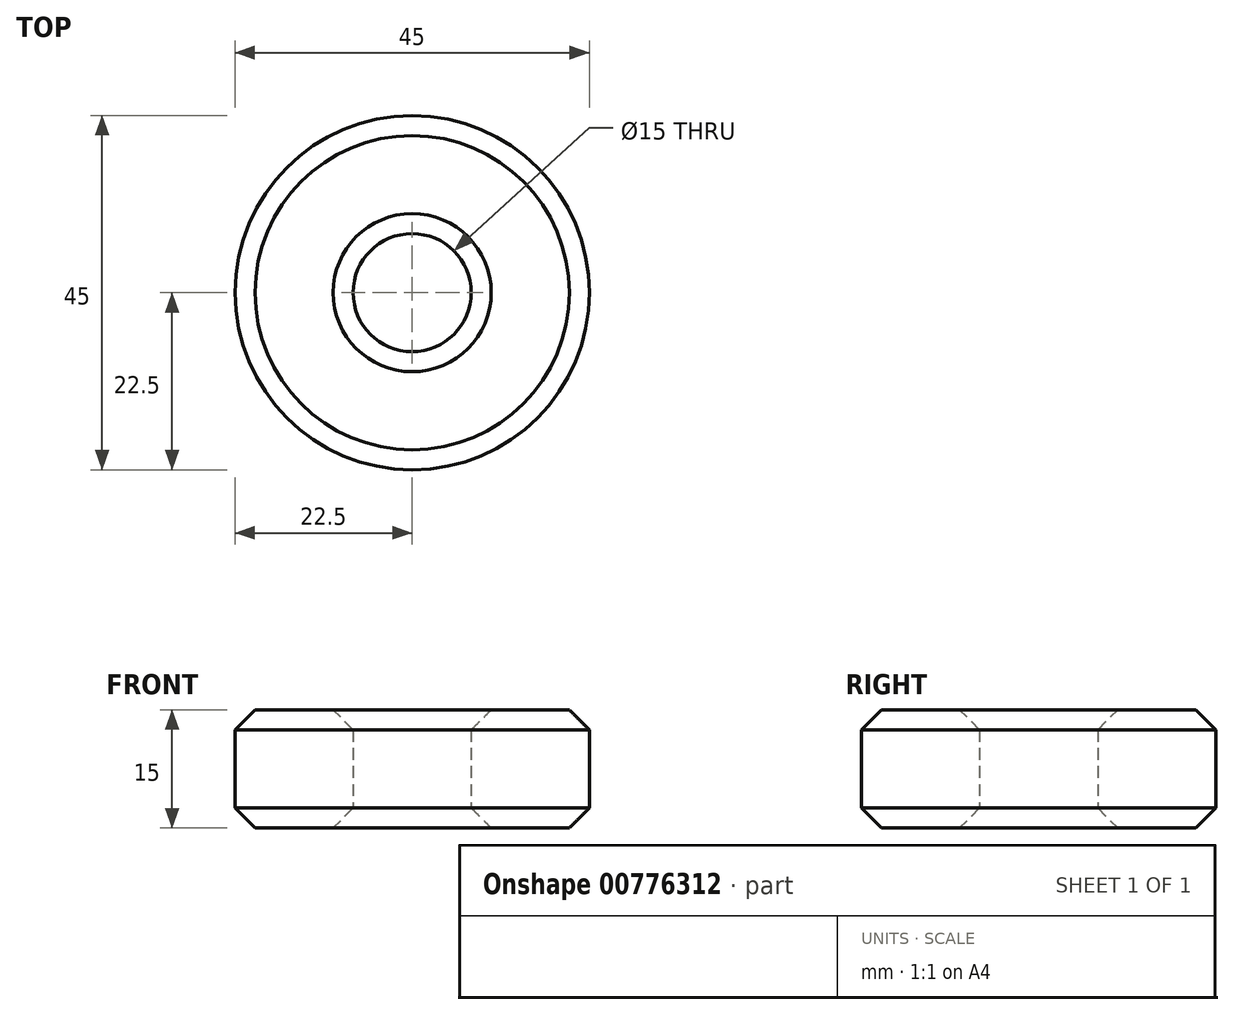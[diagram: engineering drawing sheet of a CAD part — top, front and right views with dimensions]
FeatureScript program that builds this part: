
annotation { "Feature Type Name" : "Feature", "Feature Type Description" : "" }
export const myFeature = defineFeature(function(context is Context, id is Id, definition is map)
    precondition{}
    {
        {
            var Q0;
            Q0=qCreatedBy(makeId("Top.planeOp"),FACE);
            var sketch = newSketch(context, id + "F0", { "sketchPlane" : qUnion([Q0])});
            skCircle(sketch, "E0", {"center": v(0, 0) * mm, "radius": 7.5 * mm});
            skCircle(sketch, "E1", {"center": v(0, 0) * mm, "radius": 22.5 * mm});
            skSolve(sketch);
        }
        {
            var Q0;
            Q0 = qSketchRegion(id + "F0", true);
            extrude(context, id + "F1", {"entities" : qUnion([Q0]), "depth" : 15 * mm, "offsetDistance" : 25.4 * mm});
        }
        {
            var Q0;
            Q0=makeQuery(id+"F1.opExtrude","CAP_EDGE",EDGE,{"disambiguationData":[OSD([sQuery(id+"F0.wireOp",EDGE,"E1")])],"isStart":false});
            var Q1;
            Q1=makeQuery(id+"F1.opExtrude","CAP_EDGE",EDGE,{"disambiguationData":[OSD([sQuery(id+"F0.wireOp",EDGE,"E1")])],"isStart":true});
            var Q2;
            Q2=makeQuery(id+"F1.opExtrude","CAP_EDGE",EDGE,{"disambiguationData":[OSD([sQuery(id+"F0.wireOp",EDGE,"E0")])],"isStart":false});
            var Q3;
            Q3=makeQuery(id+"F1.opExtrude","CAP_EDGE",EDGE,{"disambiguationData":[OSD([sQuery(id+"F0.wireOp",EDGE,"E0")])],"isStart":true});
            chamfer(context, id + "F2", {"entities" : qUnion([Q0, Q1, Q2, Q3]), "chamferType" : ChamferType.OFFSET_ANGLE, "width" : 2.54 * mm, "oppositeDirection" : false, "angle" : 45 * degree, "tangentPropagation" : true});
        }
    });
